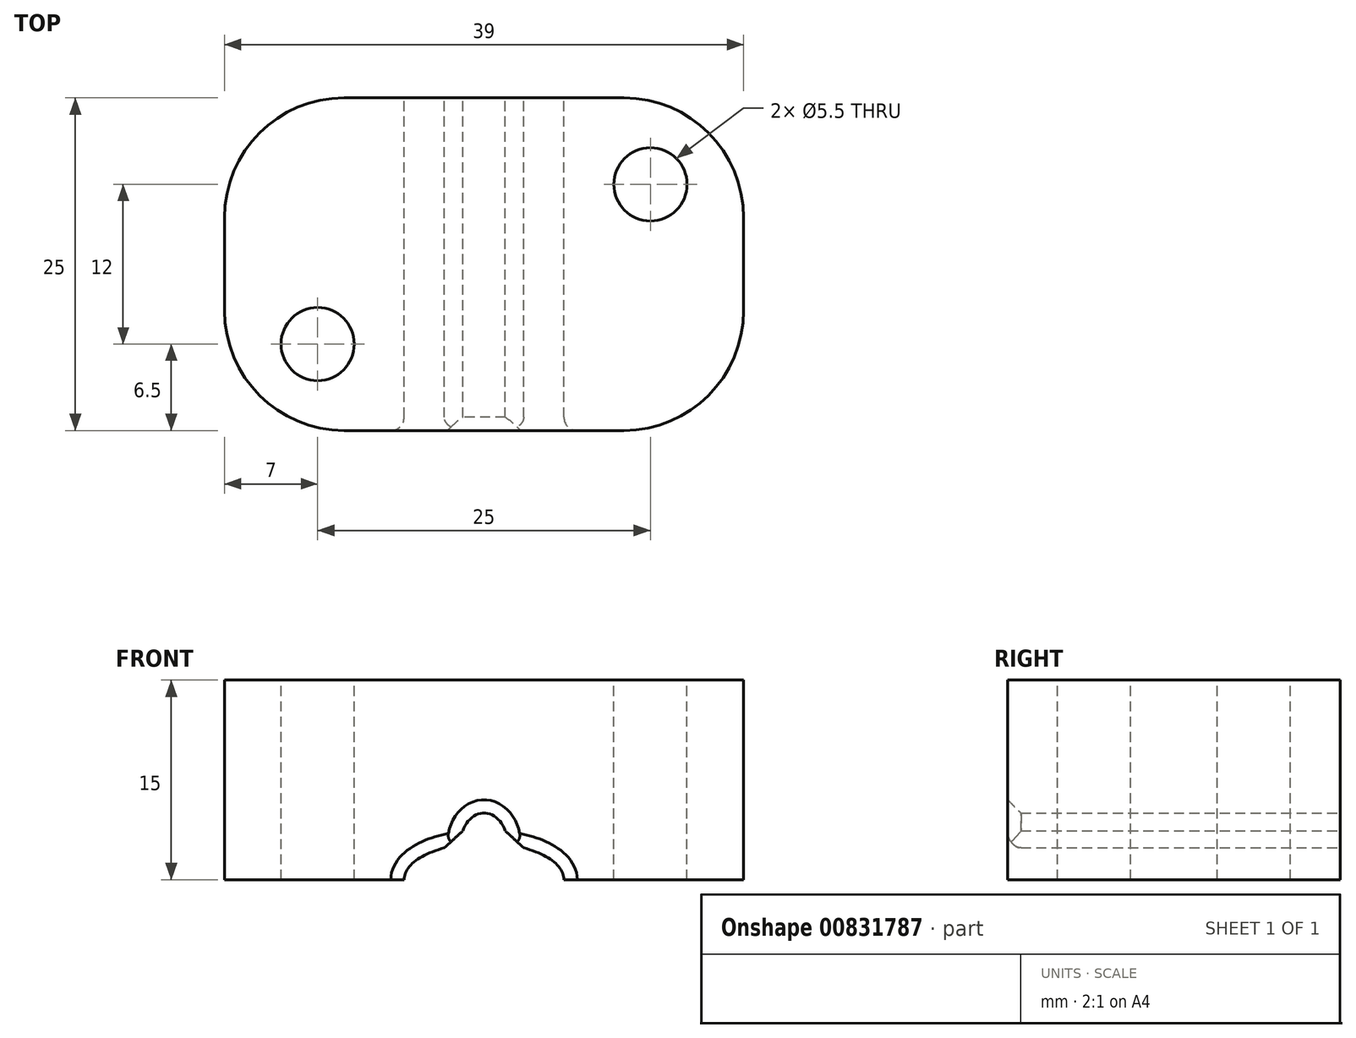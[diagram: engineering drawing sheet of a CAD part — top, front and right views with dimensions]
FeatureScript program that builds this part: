
annotation { "Feature Type Name" : "Feature", "Feature Type Description" : "" }
export const myFeature = defineFeature(function(context is Context, id is Id, definition is map)
    precondition{}
    {
        {
            var Q0;
            Q0=qCreatedBy(makeId("Top.planeOp"),FACE);
            var sketch = newSketch(context, id + "F0", { "sketchPlane" : qUnion([Q0])});
            skLineSegment(sketch, "E0.bottom", {"start": v(19.5, 12.5) * mm, "end": v(-19.5, 12.5) * mm});
            skLineSegment(sketch, "E0.top", {"start": v(19.5, -12.5) * mm, "end": v(-19.5, -12.5) * mm});
            skLineSegment(sketch, "E0.left", {"start": v(19.5, 12.5) * mm, "end": v(19.5, -12.5) * mm});
            skLineSegment(sketch, "E0.right", {"start": v(-19.5, 12.5) * mm, "end": v(-19.5, -12.5) * mm});
            skPoint(sketch, "E0.middle", {"position": v(0, 0) * mm});
            skSolve(sketch);
        }
        {
            var Q0;
            Q0 = qSketchRegion(id + "F0", true);
            extrude(context, id + "F1", {"entities" : qUnion([Q0]), "depth" : 15 * mm, "offsetDistance" : 25 * mm});
        }
        {
            var Q0;
            Q0=makeQuery(id+"F1.opExtrude","SWEPT_EDGE",EDGE,{"disambiguationData":[OSD([sQuery(id+"F0.wireOp",EDGE,"E0.bottom"),sQuery(id+"F0.wireOp",EDGE,"E0.left")])]});
            var Q1;
            Q1=makeQuery(id+"F1.opExtrude","SWEPT_EDGE",EDGE,{"disambiguationData":[OSD([sQuery(id+"F0.wireOp",EDGE,"E0.bottom"),sQuery(id+"F0.wireOp",EDGE,"E0.right")])]});
            var Q2;
            Q2=makeQuery(id+"F1.opExtrude","SWEPT_EDGE",EDGE,{"disambiguationData":[OSD([sQuery(id+"F0.wireOp",EDGE,"E0.top"),sQuery(id+"F0.wireOp",EDGE,"E0.right")])]});
            var Q3;
            Q3=makeQuery(id+"F1.opExtrude","SWEPT_EDGE",EDGE,{"disambiguationData":[OSD([sQuery(id+"F0.wireOp",EDGE,"E0.top"),sQuery(id+"F0.wireOp",EDGE,"E0.left")])]});
            fillet(context, id + "F2", {"entities" : qUnion([Q0, Q1, Q2, Q3]), "radius" : 9 * mm, "tangentPropagation" : true, "allowEdgeOverflow" : false});
        }
        {
            var Q0;
            Q0=makeQuery(id+"F1.opExtrude","SWEPT_FACE",FACE,{"disambiguationData":[OSD([sQuery(id+"F0.wireOp",EDGE,"E0.bottom")])]});
            var sketch = newSketch(context, id + "F3", { "sketchPlane" : qUnion([Q0])});
            skEllipse(sketch, "E1", {"center": v(0, 0) * mm, "majorRadius": 6 * mm, "minorRadius": 2.75 * mm, "majorAxis": v(-1, 0)});
            skSolve(sketch);
        }
        {
            var Q0;
            Q0 = qSketchRegion(id + "F3", true);
            var Q1;
            Q1=makeQuery(id+"F1.opExtrude","SWEPT_FACE",FACE,{"disambiguationData":[OSD([sQuery(id+"F0.wireOp",EDGE,"E0.top")])]});
            extrude(context, id + "F4", {"entities" : qUnion([Q0, Q1]), "operationType" : NewBodyOperationType.REMOVE, "endBound" : BoundingType.THROUGH_ALL, "oppositeDirection" : true, "depth" : 25 * mm, "offsetDistance" : 25 * mm});
        }
        {
            var Q0;
            Q0=makeQuery(id+"F1.opExtrude","SWEPT_FACE",FACE,{"disambiguationData":[OSD([sQuery(id+"F0.wireOp",EDGE,"E0.bottom")])]});
            var sketch = newSketch(context, id + "F5", { "sketchPlane" : qUnion([Q0])});
            skEllipse(sketch, "E2", {"center": v(0, 2.75) * mm, "majorRadius": 2.25 * mm, "minorRadius": 1.75 * mm, "majorAxis": v(0, 1)});
            skSolve(sketch);
        }
        {
            var Q0;
            Q0 = qSketchRegion(id + "F5", true);
            extrude(context, id + "F6", {"entities" : qUnion([Q0]), "operationType" : NewBodyOperationType.REMOVE, "endBound" : BoundingType.THROUGH_ALL, "oppositeDirection" : true, "depth" : 25 * mm, "offsetDistance" : 25 * mm});
        }
        {
            var Q0;
            Q0=makeQuery(id+"F1.opExtrude","CAP_FACE",FACE,{"disambiguationData":[OSD([sQuery(id+"F0.wireOp",EDGE,"E0.bottom"),sQuery(id+"F0.wireOp",EDGE,"E0.top"),sQuery(id+"F0.wireOp",EDGE,"E0.left"),sQuery(id+"F0.wireOp",EDGE,"E0.right")])],"isStart":false});
            var sketch = newSketch(context, id + "F7", { "sketchPlane" : qUnion([Q0])});
            skCircle(sketch, "E3", {"center": v(-12.5, -6) * mm, "radius": 2.75 * mm});
            skCircle(sketch, "E4", {"center": v(12.5, 6) * mm, "radius": 2.75 * mm});
            skSolve(sketch);
        }
        {
            var Q0;
            Q0 = qSketchRegion(id + "F7", true);
            extrude(context, id + "F8", {"entities" : qUnion([Q0]), "operationType" : NewBodyOperationType.REMOVE, "endBound" : BoundingType.THROUGH_ALL, "oppositeDirection" : true, "depth" : 25 * mm, "offsetDistance" : 25 * mm});
        }
        {
            var Q0;
            Q0=makeQuery(id+"F6.boolean.opBoolean","COPY",EDGE,{"derivedFrom":makeQuery(id+"F6.opExtrude","CAP_EDGE",EDGE,{"disambiguationData":[OSD([sQuery(id+"F5.wireOp",EDGE,"E2")])],"isStart":true})});
            var Q1;
            Q1=makeQuery(id+"F6.boolean.opBoolean","INTERSECT",EDGE,{"derivedFrom":[makeQuery(id+"F1.opExtrude","SWEPT_FACE",FACE,{"disambiguationData":[OSD([sQuery(id+"F0.wireOp",EDGE,"E0.top")])]}),makeQuery(id+"F6.opExtrude","SWEPT_FACE",FACE,{"disambiguationData":[OSD([sQuery(id+"F5.wireOp",EDGE,"E2")])]})]});
            chamfer(context, id + "F9", {"entities" : qUnion([Q0, Q1]), "width" : 1 * mm, "tangentPropagation" : true});
        }
        {
            var Q0;
            Q0=makeQuery(id+"F6.boolean.opBoolean","INTERSECT",EDGE,{"disambiguationData":[OD(0.0)],"derivedFrom":[makeQuery(id+"F4.boolean.opBoolean","COPY",FACE,{"derivedFrom":makeQuery(id+"F4.opExtrude","SWEPT_FACE",FACE,{"disambiguationData":[OSD([sQuery(id+"F3.wireOp",EDGE,"E1")])]})}),makeQuery(id+"F6.opExtrude","SWEPT_FACE",FACE,{"disambiguationData":[OSD([sQuery(id+"F5.wireOp",EDGE,"E2")])]})]});
            var Q1;
            Q1=makeQuery(id+"F6.boolean.opBoolean","INTERSECT",EDGE,{"disambiguationData":[OD(1.0)],"derivedFrom":[makeQuery(id+"F4.boolean.opBoolean","COPY",FACE,{"derivedFrom":makeQuery(id+"F4.opExtrude","SWEPT_FACE",FACE,{"disambiguationData":[OSD([sQuery(id+"F3.wireOp",EDGE,"E1")])]})}),makeQuery(id+"F6.opExtrude","SWEPT_FACE",FACE,{"disambiguationData":[OSD([sQuery(id+"F5.wireOp",EDGE,"E2")])]})]});
            chamfer(context, id + "F10", {"entities" : qUnion([Q0, Q1]), "width" : 2 * mm, "tangentPropagation" : true});
        }
        {
            var Q0;
            Q0=makeQuery(id+"F6.boolean.opBoolean","SPLIT",EDGE,{"disambiguationData":[OD(0.0)],"derivedFrom":makeQuery(id+"F4.boolean.opBoolean","COPY",EDGE,{"derivedFrom":makeQuery(id+"F4.opExtrude","CAP_EDGE",EDGE,{"disambiguationData":[OSD([sQuery(id+"F3.wireOp",EDGE,"E1")])],"isStart":true})})});
            var Q1;
            Q1=makeQuery(id+"F6.boolean.opBoolean","SPLIT",EDGE,{"disambiguationData":[OD(1.0)],"derivedFrom":makeQuery(id+"F4.boolean.opBoolean","COPY",EDGE,{"derivedFrom":makeQuery(id+"F4.opExtrude","CAP_EDGE",EDGE,{"disambiguationData":[OSD([sQuery(id+"F3.wireOp",EDGE,"E1")])],"isStart":true})})});
            var Q2;
            {var subQ0=sQuery(id+"F0.wireOp",EDGE,"E0.top");Q2=makeQuery(id+"F6.boolean.opBoolean","SPLIT",EDGE,{"disambiguationData":[OD(0.0)],"derivedFrom":makeQuery(id+"F4.boolean.opBoolean","INTERSECT",EDGE,{"derivedFrom":[makeQuery(id+"F1.opExtrude","SWEPT_FACE",FACE,{"disambiguationData":[OSD([subQ0])]}),makeQuery(id+"F4.opExtrude","CAP_FACE",FACE,{"disambiguationData":[OSD([subQ0])],"isStart":true}),makeQuery(id+"F4.opExtrude","SWEPT_FACE",FACE,{"disambiguationData":[OSD([sQuery(id+"F3.wireOp",EDGE,"E1")])]})]})});}
            var Q3;
            {var subQ0=sQuery(id+"F0.wireOp",EDGE,"E0.top");Q3=makeQuery(id+"F6.boolean.opBoolean","SPLIT",EDGE,{"disambiguationData":[OD(1.0)],"derivedFrom":makeQuery(id+"F4.boolean.opBoolean","INTERSECT",EDGE,{"derivedFrom":[makeQuery(id+"F1.opExtrude","SWEPT_FACE",FACE,{"disambiguationData":[OSD([subQ0])]}),makeQuery(id+"F4.opExtrude","CAP_FACE",FACE,{"disambiguationData":[OSD([subQ0])],"isStart":true}),makeQuery(id+"F4.opExtrude","SWEPT_FACE",FACE,{"disambiguationData":[OSD([sQuery(id+"F3.wireOp",EDGE,"E1")])]})]})});}
            fillet(context, id + "F11", {"entities" : qUnion([Q0, Q1, Q2, Q3]), "radius" : 1 * mm, "tangentPropagation" : true, "allowEdgeOverflow" : false});
        }
    });
